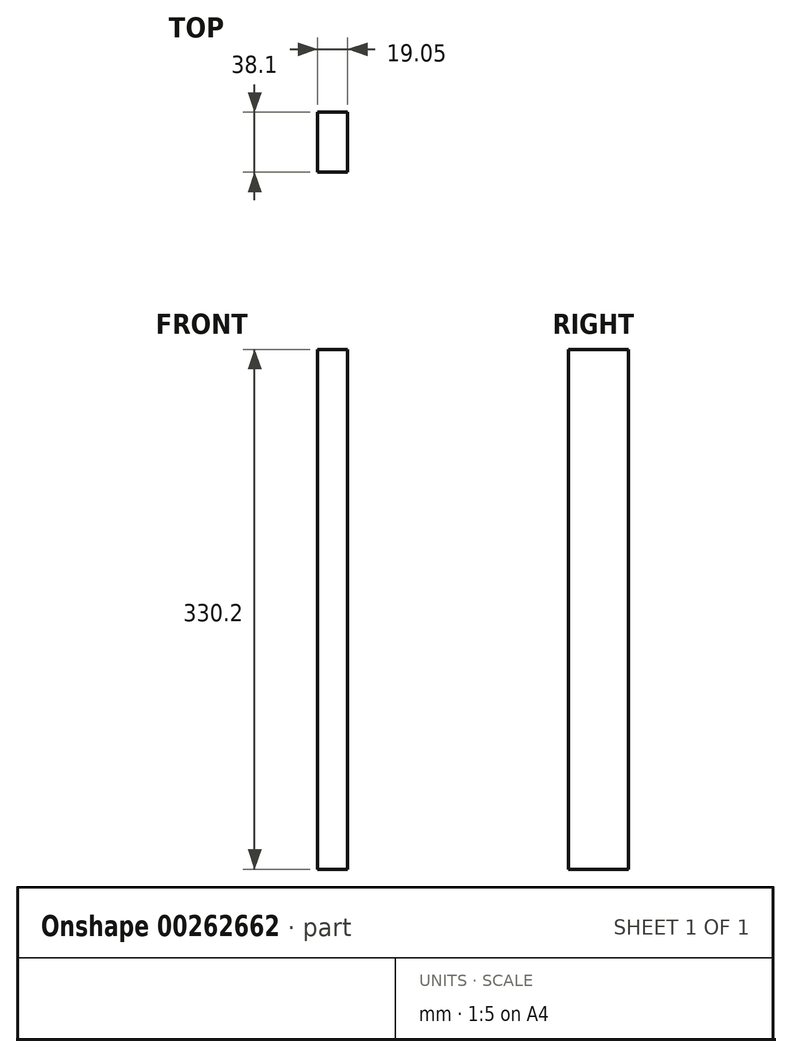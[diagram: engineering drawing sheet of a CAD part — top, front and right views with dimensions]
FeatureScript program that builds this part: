
annotation { "Feature Type Name" : "Feature", "Feature Type Description" : "" }
export const myFeature = defineFeature(function(context is Context, id is Id, definition is map)
    precondition{}
    {
        {
            var Q0;
            Q0=qCreatedBy(makeId("Front.planeOp"),FACE);
            var sketch = newSketch(context, id + "F0", { "sketchPlane" : qUnion([Q0])});
            skLineSegment(sketch, "E0", {"start": v(0, 0) * mm, "end": v(-19.05, 0) * mm});
            skLineSegment(sketch, "E1", {"start": v(-19.05, 0) * mm, "end": v(-19.05, -330.2) * mm});
            skLineSegment(sketch, "E2", {"start": v(-19.05, -330.2) * mm, "end": v(0, -330.2) * mm});
            skLineSegment(sketch, "E3", {"start": v(0, -330.2) * mm, "end": v(0, 0) * mm});
            skSolve(sketch);
        }
        {
            var Q0;
            Q0=makeQuery(id+"F0.imprint","IMPRINT",FACE,{"disambiguationData":[TD([[makeQuery(id+"F0.imprint","IMPRINT",EDGE,{"derivedFrom":sQuery(id+"F0.wireOp",EDGE,"E0")}),1.0]])]});
            extrude(context, id + "F1", {"entities" : qUnion([Q0]), "offsetDistance" : 25.4 * mm, "depth" : 38.1 * mm});
        }
    });
